# Revit family: Urinal-Top_Spud-Acorn-Penal-Ware-2180-T-3
name_source: partatom
category: Plumbing Fixtures
units: mm (PartAtom-declared; Revit-internal decimal feet)

## family parameters
Cut with Voids When Loaded = No
Host = Face
OmniClass Number = 23.45.05.21.11.21
OmniClass Title = Urinals
Part Type = Normal
Room Calculation Point = No
Round Connector Dimension = Use Diameter
Shared = Yes

## types (1)
- 2180-T-3
    1.0 GPF = Yes
    1.5 GPF = No
    3 - On-Floor, Floor Outlet = Yes
    ADA Compliant = Yes
    Assembly Code = D2010210
    Beehive Strainer = Yes
    CFR Continuous Flushing Rim = No
    CW Connection = Yes
    CWFU = 5
    Cold Water Connection Diameter = 3/4"
    Cold Water Connection Height = 49 1/2"
    Cold Water Connection Radius = 3/8"
    Cold Water Connection Width = 4 3/4"
    Default Elevation = 0"
    Description = Front Mount, Stall Type ADA Compliant Stainless Steel
    EG Enviro-Glaze, Specify Color = No
    FV Flush Valve, Mechanical (N/A for ADA) = No
    FVBO Flush Valve by Others = No
    FVH Flush Valve, Hydraulic (N/A for Top Supply) = No
    FVL Flush Valve, Lever Handle (Wall Supply) = No
    FVT Flush Valve Thru Wall Connector = No
    Finish = Stainless Steel-Acorn-Satin
    Flush Rate = 1.0 GPF
    Flush Valve Specification = Specify Flush Valve
    Flush Valve Visibility = Yes
    HW Connection = No
    HWFU = 0
    Height = 42"
    Installation Instruction Link = https://www.acorneng.com
    Installation Type = Wall Mount
    Length = 15"
    MVCFV Time-Trol® Electronic Flush Valve = No
    Manufacturer = Acorn Engineering
    Material = Stainless Steel-Acorn-Satin
    Model = 2180-T-3
    Price = Prices may vary. Please consult Manufacturer Representative for most up-to-date price list.
    Product Documentation Link = https://www.acorneng.com
    Product Page URL = https://www.acorneng.com
    Revised Date = 12/27/2024
    T - Top (Exposed) = Yes
    TF Transformer, 120VAC to 24VAC (-MVCFV option) = No
    URL = https://acorneng.com
    Urinal Waste Outlet = Yes
    Vent Connection = No
    Visbility = Specify Flush Valve : Must Match "Model" Value
    WFU = 5
    Wall Mounting Hardware = Yes
    Waste Connection = Yes
    Waste Connection Diameter = 2"
    Waste Connection Radius = 1"
    Width = 18"

## geometry (parser evidence)
native form markers: Sweep x4
no freeform markers — native parametric forms only
